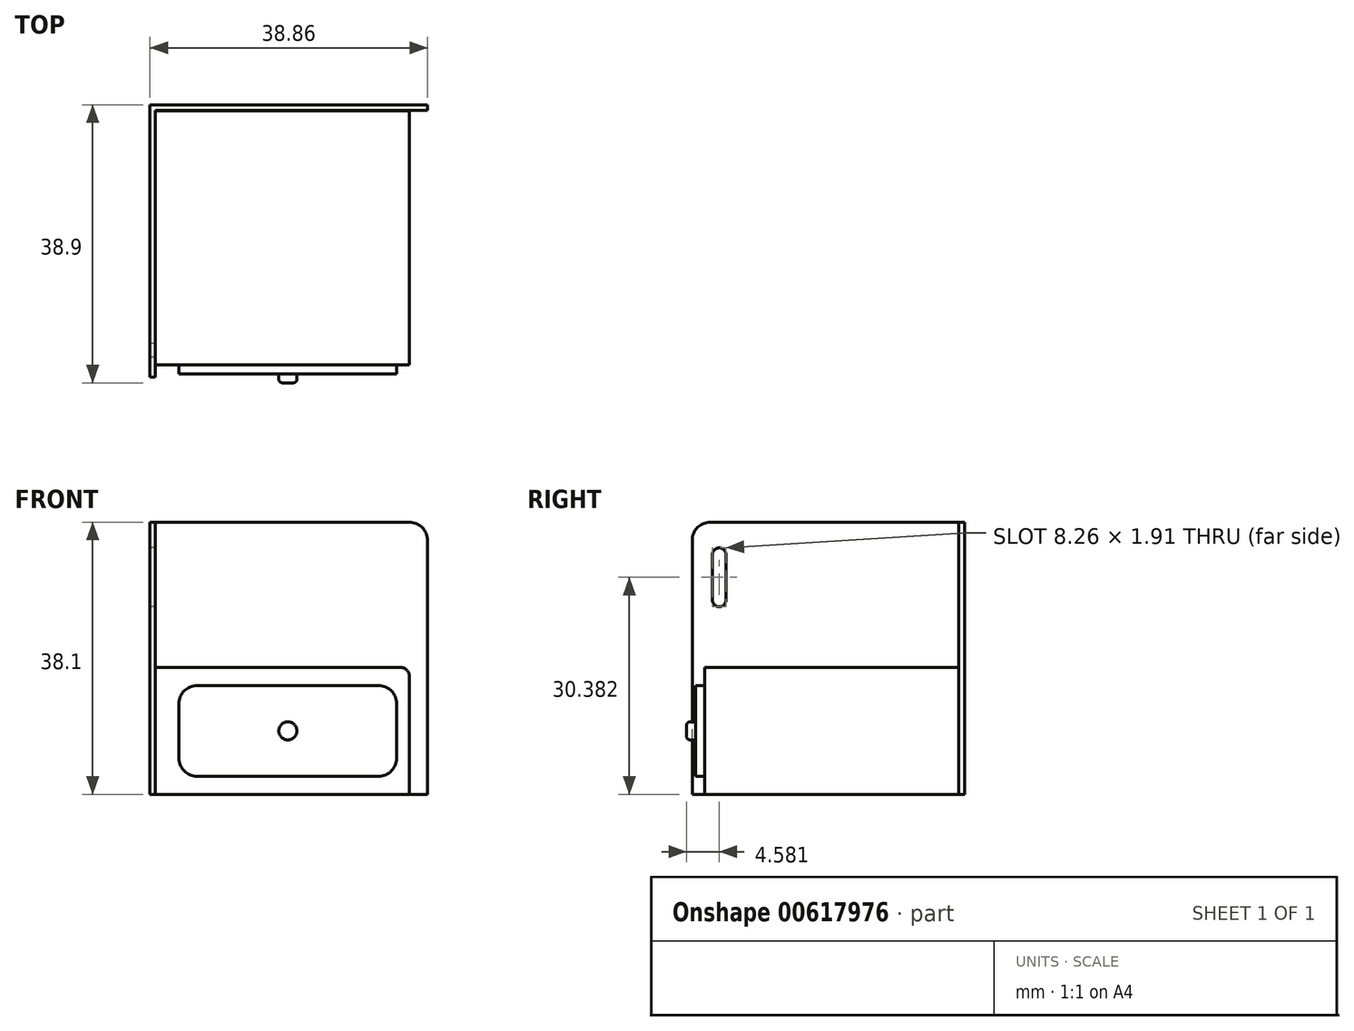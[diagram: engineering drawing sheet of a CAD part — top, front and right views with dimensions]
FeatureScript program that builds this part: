
annotation { "Feature Type Name" : "Feature", "Feature Type Description" : "" }
export const myFeature = defineFeature(function(context is Context, id is Id, definition is map)
    precondition{}
    {
        {
            var Q0;
            Q0=qCreatedBy(makeId("Right.planeOp"),FACE);
            var sketch = newSketch(context, id + "F0", { "sketchPlane" : qUnion([Q0])});
            skLineSegment(sketch, "E0.bottom", {"start": v(0, 0) * mm, "end": v(-38.1, 0) * mm});
            skLineSegment(sketch, "E0.top", {"start": v(0, 38.1) * mm, "end": v(-38.1, 38.1) * mm});
            skLineSegment(sketch, "E0.left", {"start": v(0, 0) * mm, "end": v(0, 38.1) * mm});
            skLineSegment(sketch, "E0.right", {"start": v(-38.1, 0) * mm, "end": v(-38.1, 38.1) * mm});
            skSolve(sketch);
        }
        {
            var Q0;
            Q0=qCreatedBy(makeId("Front.planeOp"),FACE);
            var sketch = newSketch(context, id + "F1", { "sketchPlane" : qUnion([Q0])});
            skLineSegment(sketch, "E1.0", {"start": v(0, 0) * mm, "end": v(0, 38.1) * mm});
            skLineSegment(sketch, "E2.bottom", {"start": v(0, 38.1) * mm, "end": v(38.1, 38.1) * mm});
            skLineSegment(sketch, "E2.top", {"start": v(0, 0) * mm, "end": v(38.1, 0) * mm});
            skLineSegment(sketch, "E2.left", {"start": v(0, 38.1) * mm, "end": v(0, 0) * mm});
            skLineSegment(sketch, "E2.right", {"start": v(38.1, 38.1) * mm, "end": v(38.1, 0) * mm});
            skLineSegment(sketch, "E3.bottom", {"start": v(38.1, 38.1) * mm, "end": v(76.2, 38.1) * mm});
            skLineSegment(sketch, "E3.top", {"start": v(38.1, 0) * mm, "end": v(76.2, 0) * mm});
            skLineSegment(sketch, "E3.right", {"start": v(76.2, 38.1) * mm, "end": v(76.2, 0) * mm});
            skSolve(sketch);
        }
        {
            var Q0;
            Q0=makeQuery(id+"F0.imprint","IMPRINT",FACE,{"disambiguationData":[TD([[makeQuery(id+"F0.imprint","IMPRINT",EDGE,{"derivedFrom":sQuery(id+"F0.wireOp",EDGE,"E0.bottom")}),-1.0]])]});
            extrude(context, id + "F2", {"entities" : qUnion([Q0]), "oppositeDirection" : true, "depth" : 0.76 * mm, "offsetDistance" : 25.4 * mm});
        }
        {
            var Q0;
            Q0=makeQuery(id+"F1.imprint","IMPRINT",FACE,{"disambiguationData":[TD([[makeQuery(id+"F1.imprint","IMPRINT",EDGE,{"derivedFrom":sQuery(id+"F1.wireOp",EDGE,"E2.bottom")}),-1.0]])]});
            extrude(context, id + "F3", {"entities" : qUnion([Q0]), "operationType" : NewBodyOperationType.ADD, "depth" : 0.76 * mm, "offsetDistance" : 25.4 * mm});
        }
        {
            var Q0;
            Q0=qCreatedBy(makeId("Top.planeOp"),FACE);
            var sketch = newSketch(context, id + "F4", { "sketchPlane" : qUnion([Q0])});
            skPoint(sketch, "E4.0", {"position": v(0, -0.8) * mm});
            skLineSegment(sketch, "E5.bottom", {"start": v(0, -0.8) * mm, "end": v(35.56, -0.8) * mm});
            skLineSegment(sketch, "E5.top", {"start": v(0, -36.36) * mm, "end": v(35.56, -36.36) * mm});
            skLineSegment(sketch, "E5.left", {"start": v(0, -0.8) * mm, "end": v(0, -36.36) * mm});
            skLineSegment(sketch, "E5.right", {"start": v(35.56, -0.8) * mm, "end": v(35.56, -36.36) * mm});
            skSolve(sketch);
        }
        {
            var Q0;
            Q0=makeQuery(id+"F4.imprint","IMPRINT",FACE,{"disambiguationData":[TD([[makeQuery(id+"F4.imprint","IMPRINT",EDGE,{"derivedFrom":sQuery(id+"F4.wireOp",EDGE,"E5.bottom")}),-1.0]])]});
            extrude(context, id + "F5", {"entities" : qUnion([Q0]), "depth" : 17.78 * mm});
        }
        {
            var Q0;
            Q0=makeQuery(id+"F5.opExtrude","SWEPT_FACE",FACE,{"disambiguationData":[OSD([sQuery(id+"F4.wireOp",EDGE,"E5.top")])]});
            var sketch = newSketch(context, id + "F6", { "sketchPlane" : qUnion([Q0])});
            skLineSegment(sketch, "E6.0", {"start": v(35.56, 17.78) * mm, "end": v(35.56, 0) * mm});
            skLineSegment(sketch, "E7.0.2", {"start": v(35.56, 17.78) * mm, "end": v(0, 17.78) * mm});
            skLineSegment(sketch, "E7.0.3", {"start": v(0, 17.78) * mm, "end": v(0, 0) * mm});
            skLineSegment(sketch, "E8.bottom", {"start": v(33.78, 15.24) * mm, "end": v(3.3, 15.24) * mm});
            skLineSegment(sketch, "E8.top", {"start": v(33.78, 2.54) * mm, "end": v(3.3, 2.54) * mm});
            skLineSegment(sketch, "E8.left", {"start": v(33.78, 15.24) * mm, "end": v(33.78, 2.54) * mm});
            skLineSegment(sketch, "E8.right", {"start": v(3.3, 15.24) * mm, "end": v(3.3, 2.54) * mm});
            skPoint(sketch, "E8.middle", {"position": v(18.54, 8.9) * mm});
            skSolve(sketch);
        }
        {
            var Q0;
            Q0=makeQuery(id+"F6.imprint","IMPRINT",FACE,{"disambiguationData":[TD([[makeQuery(id+"F6.imprint","IMPRINT",EDGE,{"derivedFrom":sQuery(id+"F6.wireOp",EDGE,"E8.bottom")}),1.0]])]});
            extrude(context, id + "F7", {"entities" : qUnion([Q0]), "depth" : 1.27 * mm});
        }
        {
            var Q0;
            Q0=makeQuery(id+"F7.opExtrude","CAP_FACE",FACE,{"disambiguationData":[OSD([sQuery(id+"F6.wireOp",EDGE,"E8.bottom"),sQuery(id+"F6.wireOp",EDGE,"E8.top"),sQuery(id+"F6.wireOp",EDGE,"E8.left"),sQuery(id+"F6.wireOp",EDGE,"E8.right")])],"isStart":false});
            var sketch = newSketch(context, id + "F8", { "sketchPlane" : qUnion([Q0])});
            skCircle(sketch, "E9", {"center": v(18.54, 8.89) * mm, "radius": 1.27 * mm});
            skSolve(sketch);
        }
        {
            var Q0;
            Q0=makeQuery(id+"F8.imprint","IMPRINT",FACE,{"disambiguationData":[TD([[makeQuery(id+"F8.imprint","IMPRINT",EDGE,{"derivedFrom":sQuery(id+"F8.wireOp",EDGE,"E9")}),1.0]])]});
            extrude(context, id + "F9", {"entities" : qUnion([Q0]), "depth" : 1.27 * mm});
        }
        {
            var Q0;
            Q0=makeQuery(id+"F2.opExtrude","SWEPT_EDGE",EDGE,{"disambiguationData":[OSD([sQuery(id+"F0.wireOp",EDGE,"E0.top"),sQuery(id+"F0.wireOp",EDGE,"E0.right")])]});
            fillet(context, id + "F10", {"entities" : qUnion([Q0]), "radius" : 2.54 * mm, "tangentPropagation" : true, "allowEdgeOverflow" : false});
        }
        {
            var Q0;
            Q0=makeQuery(id+"FHx2Fadl2aLvgQC_2.opExtrude","SWEPT_EDGE",EDGE,{"disambiguationData":[OSD([sQuery(id+"FUhdUntOpQ8Ue4B_2.wireOp",EDGE,"hsLLnVC4-a2HW-eBwm-Imrp-P71soF4f9oXD.top"),sQuery(id+"FUhdUntOpQ8Ue4B_2.wireOp",EDGE,"hsLLnVC4-a2HW-eBwm-Imrp-P71soF4f9oXD.right")])]});
            var Q1;
            Q1=makeQuery(id+"F5.opExtrude","CAP_EDGE",EDGE,{"disambiguationData":[OSD([sQuery(id+"F4.wireOp",EDGE,"E5.right")])],"isStart":false});
            fillet(context, id + "F11", {"entities" : qUnion([Q0, Q1]), "radius" : 1.27 * mm, "tangentPropagation" : true, "allowEdgeOverflow" : false});
        }
        {
            var Q0;
            Q0=makeQuery(id+"F2.opExtrude","CAP_FACE",FACE,{"disambiguationData":[OSD([sQuery(id+"F0.wireOp",EDGE,"E0.bottom"),sQuery(id+"F0.wireOp",EDGE,"E0.top"),sQuery(id+"F0.wireOp",EDGE,"E0.left"),sQuery(id+"F0.wireOp",EDGE,"E0.right")])],"isStart":false});
            var sketch = newSketch(context, id + "F12", { "sketchPlane" : qUnion([Q0])});
            skLineSegment(sketch, "E10.left", {"start": v(33.37, 33.56) * mm, "end": v(33.37, 27.2) * mm});
            skLineSegment(sketch, "E10.right", {"start": v(35.27, 33.56) * mm, "end": v(35.27, 27.2) * mm});
            skArc(sketch, "E11", {"start": v(35.27, 33.56) * mm, "mid": v(34.32, 34.5) * mm, "end": v(33.37, 33.56) * mm});
            skArc(sketch, "E12", {"start": v(33.37, 27.2) * mm, "mid": v(34.32, 26.25) * mm, "end": v(35.27, 27.2) * mm});
            skSolve(sketch);
        }
        {
            var Q0;
            Q0=qSketchRegion(id+"F12",true);
            extrude(context, id + "F13", {"entities" : qUnion([Q0]), "operationType" : NewBodyOperationType.REMOVE, "oppositeDirection" : true, "depth" : 25.4 * mm, "offsetDistance" : 25.4 * mm});
        }
        {
            var Q0;
            Q0=makeQuery(id+"F9.opExtrude","CAP_FACE",FACE,{"disambiguationData":[OSD([sQuery(id+"F8.wireOp",EDGE,"E9")])],"isStart":false});
            fillet(context, id + "F14", {"entities" : qUnion([Q0]), "radius" : 0.5 * mm, "tangentPropagation" : true, "allowEdgeOverflow" : false});
        }
        {
            var Q0;
            Q0=makeQuery(id+"F7.opExtrude","SWEPT_EDGE",EDGE,{"disambiguationData":[OSD([sQuery(id+"F6.wireOp",EDGE,"E8.bottom"),sQuery(id+"F6.wireOp",EDGE,"E8.right")])]});
            var Q1;
            Q1=makeQuery(id+"F7.opExtrude","SWEPT_EDGE",EDGE,{"disambiguationData":[OSD([sQuery(id+"F6.wireOp",EDGE,"E8.top"),sQuery(id+"F6.wireOp",EDGE,"E8.right")])]});
            var Q2;
            Q2=makeQuery(id+"F7.opExtrude","SWEPT_EDGE",EDGE,{"disambiguationData":[OSD([sQuery(id+"F6.wireOp",EDGE,"E8.top"),sQuery(id+"F6.wireOp",EDGE,"E8.left")])]});
            var Q3;
            Q3=makeQuery(id+"F7.opExtrude","SWEPT_EDGE",EDGE,{"disambiguationData":[OSD([sQuery(id+"F6.wireOp",EDGE,"E8.bottom"),sQuery(id+"F6.wireOp",EDGE,"E8.left")])]});
            fillet(context, id + "F15", {"entities" : qUnion([Q0, Q1, Q2, Q3]), "radius" : 2.54 * mm, "tangentPropagation" : true, "allowEdgeOverflow" : false});
        }
        {
            var Q0;
            Q0=makeQuery(id+"F3.opExtrude","SWEPT_EDGE",EDGE,{"disambiguationData":[OSD([sQuery(id+"F1.wireOp",EDGE,"E2.bottom"),sQuery(id+"F1.wireOp",EDGE,"E3.bottom"),sQuery(id+"F1.wireOp",EDGE,"E2.right")])]});
            fillet(context, id + "F16", {"entities" : qUnion([Q0]), "radius" : 2.54 * mm, "tangentPropagation" : true, "allowEdgeOverflow" : false});
        }
    });
